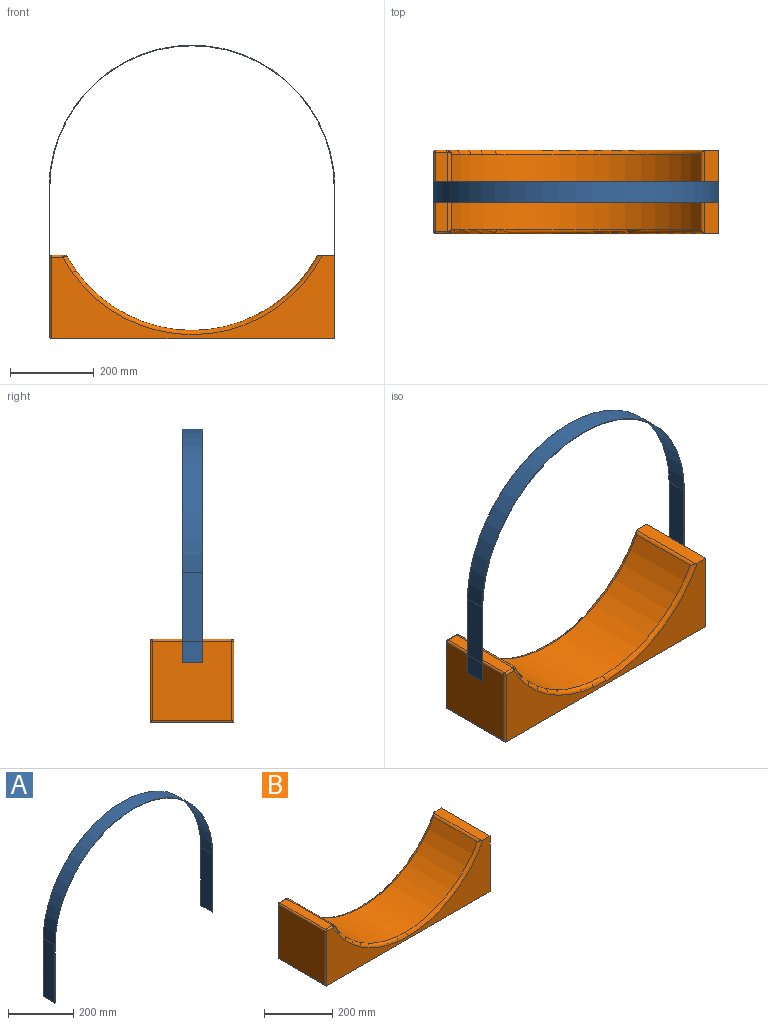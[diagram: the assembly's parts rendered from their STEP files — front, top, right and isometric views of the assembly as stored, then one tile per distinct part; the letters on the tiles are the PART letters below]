
ASSEMBLY  parts=2 mates=1
PART A: 10 faces, bbox 683x50x558.6 mm
  f0: plane 217.11x50mm, normal (-1,0,0), area 10855.7mm2, adj f1,f7,f8,f9
  f1: plane 50x1.5mm, normal (0,0,-1), area 75mm2, adj f0,f2,f8,f9
  f2: plane 217.11x50mm, normal (1,0,0), area 10855.7mm2, adj f1,f3,f8,f9
  f3: cylinder r=341.5mm len=683mm, axis (0,1,0), area 53642.7mm2, adj f2,f4,f8,f9
  f4: plane 217.11x50mm, normal (-1,0,0), area 10855.7mm2, adj f3,f5,f8,f9
  f5: plane 50x1.5mm, normal (0,0,-1), area 75mm2, adj f4,f6,f8,f9
  f6: plane 217.11x50mm, normal (1,0,0), area 10855.7mm2, adj f5,f7,f8,f9
  f7: cylinder r=340mm len=680mm, axis (0,1,0), area 53407.1mm2, adj f0,f6,f8,f9
  f8: plane 683x558.61mm, normal (0,-1,0), area 2257.1mm2, adj f0,f1,f2,f3,f4,f5,f6,f7
  f9: plane 683x558.61mm, normal (0,1,0), area 2257.1mm2, adj f0,f1,f2,f3,f4,f5,f6,f7
PART B: 24 faces, bbox 684.7x200.7x231.2 mm
  f0: cylinder r=340mm len=594.4mm, axis (0,1,0), area 130186.6mm2, adj f8,f9,f10,f11
  f1: plane 190x29.06mm, normal (0,0,1), area 5520.1mm2, adj f11,f13,f14,f18,f21,f22
  f2: plane 190x190mm, normal (-1,0,0), area 36100mm2, adj f15,f17,f18,f19
  f3: plane 675x200mm, normal (0,0,-1), area 135000mm2, adj f4,f6,f7,f17
  f4: plane 200x200mm, normal (1,0,0), area 40000mm2, adj f3,f5,f6,f7
  f5: plane 200.06x34.12mm, normal (0,0,1), area 6807.6mm2, adj f4,f6,f7,f8,f9,f10
  f6: plane 675x200mm, normal (0,-1,0), area 50419mm2, adj f3,f4,f5,f9,f14,f15
  f7: plane 675x200mm, normal (0,1,0), area 50419mm2, adj f3,f4,f5,f10,f19,f21
  f8: cylinder r=10mm len=197.6mm, axis (0,1,0), area 2018.5mm2, adj f0,f5,f9,f10
  f9: torus R=350mm, axis (0,-1,0), area 11634.6mm2, adj f0,f5,f6,f8,f12,f13
  f10: torus R=350mm, axis (0,-1,0), area 11634.6mm2, adj f0,f5,f7,f8,f22,f23
  f11: cylinder r=10mm len=188.77mm, axis (0,1,0), area 1966.2mm2, adj f0,f1,f12,f23
  f12: bspline ~10.37x9.45mm, area 40.7mm2, adj f9,f11,f13
  f13: bspline ~7.95x6.07mm, area 30.4mm2, adj f1,f9,f12,f14
  f14: cylinder r=5mm len=26.33mm, axis (1,0,0), area 206.8mm2, adj f1,f6,f13,f16
  f15: cylinder r=5mm len=195mm, axis (0,0,1), area 1517.3mm2, adj f2,f6,f16,f17
  f16: sphere r=5mm, area 39.3mm2, adj f14,f15,f18
  f17: cylinder r=5mm len=200mm, axis (0,1,0), area 1542.3mm2, adj f2,f3,f15,f19
  f18: cylinder r=5mm len=190mm, axis (0,1,0), area 1492.3mm2, adj f1,f2,f16,f20
  f19: cylinder r=5mm len=195mm, axis (0,0,-1), area 1517.3mm2, adj f2,f7,f17,f20
  f20: sphere r=5mm, area 39.3mm2, adj f18,f19,f21
  f21: cylinder r=5mm len=26.33mm, axis (-1,0,0), area 206.8mm2, adj f1,f7,f20,f22
  f22: bspline ~9.32x6.57mm, area 30.4mm2, adj f1,f10,f21,f23
  f23: bspline ~10.37x9.45mm, area 40.7mm2, adj f10,f11,f22
PLACE A t=(2.55,-4.24,238.39)mm
PLACE B t=(2.55,-3,238.39)mm fixed
MATE cylindrical A.f7 <-> B.f0  axis (0,1,0) through (2.55,-4.24,238.39)mm
